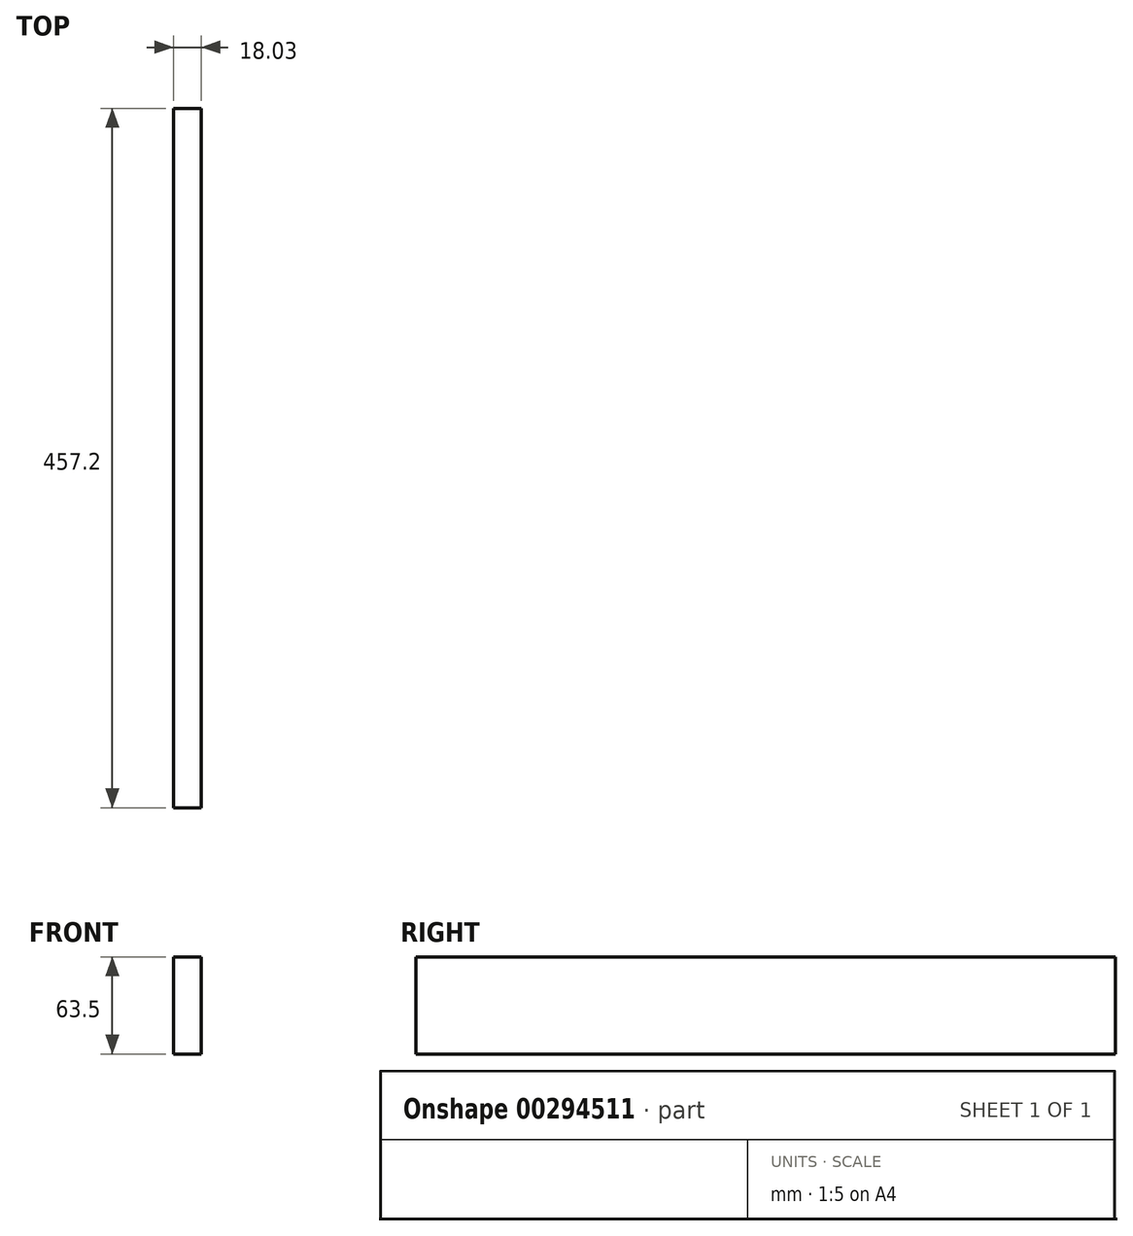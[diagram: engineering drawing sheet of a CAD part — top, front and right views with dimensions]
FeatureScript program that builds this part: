
annotation { "Feature Type Name" : "Feature", "Feature Type Description" : "" }
export const myFeature = defineFeature(function(context is Context, id is Id, definition is map)
    precondition{}
    {
        {
            var Q0;
            Q0=qCreatedBy(makeId("Right.planeOp"),FACE);
            var sketch = newSketch(context, id + "F0", { "sketchPlane" : qUnion([Q0])});
            skLineSegment(sketch, "E0.bottom", {"start": v(228.6, 31.75) * mm, "end": v(-228.6, 31.75) * mm});
            skLineSegment(sketch, "E0.top", {"start": v(228.6, -31.75) * mm, "end": v(-228.6, -31.75) * mm});
            skLineSegment(sketch, "E0.left", {"start": v(228.6, 31.75) * mm, "end": v(228.6, -31.75) * mm});
            skLineSegment(sketch, "E0.right", {"start": v(-228.6, 31.75) * mm, "end": v(-228.6, -31.75) * mm});
            skPoint(sketch, "E0.middle", {"position": v(0, 0) * mm});
            skSolve(sketch);
        }
        {
            var Q0;
            Q0=makeQuery(id+"F0.imprint","IMPRINT",FACE,{"disambiguationData":[TD([[makeQuery(id+"F0.imprint","IMPRINT",EDGE,{"derivedFrom":sQuery(id+"F0.wireOp",EDGE,"E0.bottom")}),1.0]])]});
            extrude(context, id + "F1", {"entities" : qUnion([Q0]), "depth" : 18.03 * mm});
        }
    });
